# Revit family: Haworth_Maria_Table_EU_PRELIMINARY
name_source: partatom
category: Furniture
revit_build: Autodesk Revit 2018 (Build: 20170223_1515(x64)
units: mm (PartAtom-declared; Revit-internal decimal feet)

## family parameters
Always vertical = Yes
Cut with Voids When Loaded = No
OmniClass Number = 23.40.20.00
OmniClass Title = General Furniture and Specialties
Room Calculation Point = No
Shared = No
Work Plane-Based = No

## types (1)
- Metal Top
    Actual Depth = 37 cm
    Actual Height = 80 cm
    Actual Width = 59 cm
    Assembly Code = E2020200
    Base Finish = Haworth _ Paint _ Collection White
    Description = Haworth - Maria - Table - Metal Top
    Glide Finish = Haworth _ Paint _ Collection Black
    Height = 80 cm
    Manufacturer = Haworth
    Max. Height = 80 cm
    Min. Height = 60 cm
    Model = MATA0604
    Size = Verify Final Dim. w/ Haworth
    URL = https://www.haworth.com
    URL - Product = https://www.haworth.com
    Version = 1
    Warranty = http://www.haworth.com

## geometry (parser evidence)
native form markers: Sweep x5
no freeform markers — native parametric forms only
